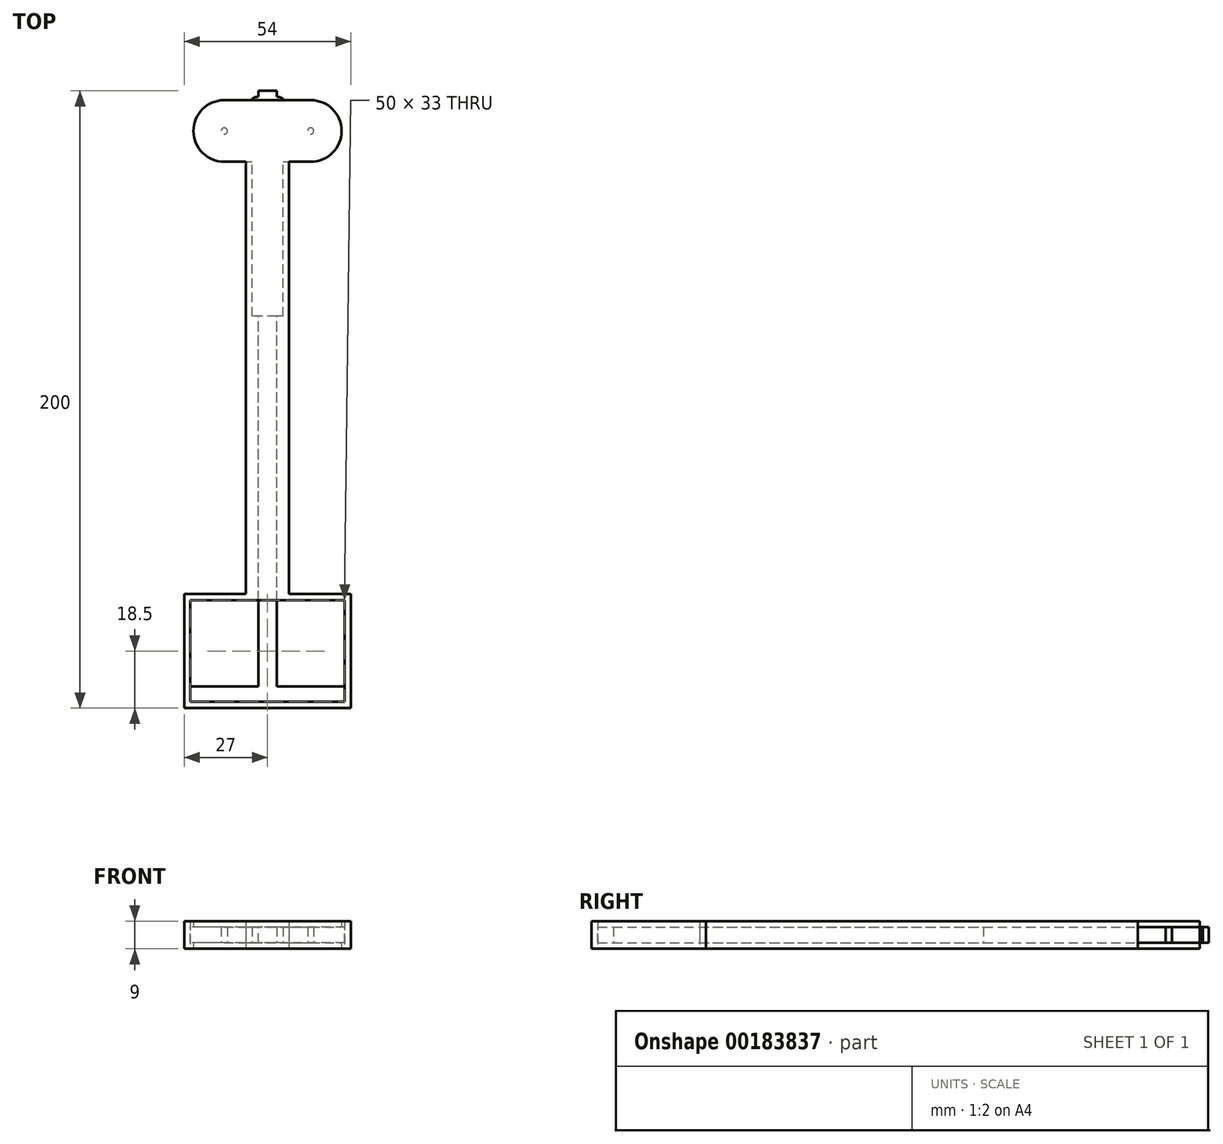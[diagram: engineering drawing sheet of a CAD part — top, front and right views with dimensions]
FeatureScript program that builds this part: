
annotation { "Feature Type Name" : "Feature", "Feature Type Description" : "" }
export const myFeature = defineFeature(function(context is Context, id is Id, definition is map)
    precondition{}
    {
        {
            var Q0;
            Q0=qCreatedBy(makeId("Top.planeOp"),FACE);
            var sketch = newSketch(context, id + "F0", { "sketchPlane" : qUnion([Q0])});
            skLineSegment(sketch, "E0.bottom", {"start": v(0, -180) * mm, "end": v(3, -180) * mm});
            skLineSegment(sketch, "E0.top", {"start": v(0, 13) * mm, "end": v(3, 13) * mm});
            skLineSegment(sketch, "E0.left", {"start": v(0, -180) * mm, "end": v(0, 13) * mm});
            skLineSegment(sketch, "E0.right", {"start": v(3, -180) * mm, "end": v(3, 13) * mm});
            skLineSegment(sketch, "E1", {"start": v(0, 10) * mm, "end": v(3, 10) * mm, "construction": true});
            skArc(sketch, "E2", {"start": v(3, 11.09) * mm, "mid": v(4.04, 10.94) * mm, "end": v(5, 10.5) * mm});
            skLineSegment(sketch, "E3", {"start": v(5, 10.5) * mm, "end": v(5, 10) * mm});
            skArc(sketch, "E4.MirrorCS", {"start": v(3, 8.91) * mm, "mid": v(4.04, 9.06) * mm, "end": v(5, 9.5) * mm});
            skLineSegment(sketch, "E5.MirrorCS", {"start": v(5, 9.5) * mm, "end": v(5, 10) * mm});
            skArc(sketch, "E6.1.0.0", {"start": v(3, 7.89) * mm, "mid": v(4.04, 7.74) * mm, "end": v(5, 7.3) * mm});
            skLineSegment(sketch, "E6.1.0.1", {"start": v(5, 7.3) * mm, "end": v(5, 6.8) * mm});
            skLineSegment(sketch, "E6.1.0.2", {"start": v(5, 6.3) * mm, "end": v(5, 6.8) * mm});
            skArc(sketch, "E6.1.0.3", {"start": v(3, 5.71) * mm, "mid": v(4.04, 5.86) * mm, "end": v(5, 6.3) * mm});
            skArc(sketch, "E6.2.0.0", {"start": v(3, 4.69) * mm, "mid": v(4.04, 4.54) * mm, "end": v(5, 4.1) * mm});
            skLineSegment(sketch, "E6.2.0.1", {"start": v(5, 4.1) * mm, "end": v(5, 3.6) * mm});
            skLineSegment(sketch, "E6.2.0.2", {"start": v(5, 3.1) * mm, "end": v(5, 3.6) * mm});
            skArc(sketch, "E6.2.0.3", {"start": v(3, 2.51) * mm, "mid": v(4.04, 2.66) * mm, "end": v(5, 3.1) * mm});
            skLineSegment(sketch, "E6.direction1", {"start": v(3, 7.39) * mm, "end": v(3, 4.19) * mm, "construction": true});
            skArc(sketch, "E7.0.3.0", {"start": v(3, 1.49) * mm, "mid": v(4.04, 1.34) * mm, "end": v(5, 0.9) * mm});
            skLineSegment(sketch, "E7.4.3.0", {"start": v(5, 0.9) * mm, "end": v(5, 0.4) * mm});
            skLineSegment(sketch, "E7.7.3.0", {"start": v(5, -0.1) * mm, "end": v(5, 0.4) * mm});
            skArc(sketch, "E7.10.3.0", {"start": v(3, -0.69) * mm, "mid": v(4.04, -0.54) * mm, "end": v(5, -0.1) * mm});
            skArc(sketch, "E7.0.4.0", {"start": v(3, -1.71) * mm, "mid": v(4.04, -1.86) * mm, "end": v(5, -2.3) * mm});
            skLineSegment(sketch, "E7.4.4.0", {"start": v(5, -2.3) * mm, "end": v(5, -2.8) * mm});
            skLineSegment(sketch, "E7.7.4.0", {"start": v(5, -3.3) * mm, "end": v(5, -2.8) * mm});
            skArc(sketch, "E7.10.4.0", {"start": v(3, -3.89) * mm, "mid": v(4.04, -3.74) * mm, "end": v(5, -3.3) * mm});
            skArc(sketch, "E7.0.5.0", {"start": v(3, -4.91) * mm, "mid": v(4.04, -5.06) * mm, "end": v(5, -5.5) * mm});
            skLineSegment(sketch, "E7.4.5.0", {"start": v(5, -5.5) * mm, "end": v(5, -6) * mm});
            skLineSegment(sketch, "E7.7.5.0", {"start": v(5, -6.5) * mm, "end": v(5, -6) * mm});
            skArc(sketch, "E7.10.5.0", {"start": v(3, -7.09) * mm, "mid": v(4.04, -6.94) * mm, "end": v(5, -6.5) * mm});
            skArc(sketch, "E7.0.6.0", {"start": v(3, -8.11) * mm, "mid": v(4.04, -8.26) * mm, "end": v(5, -8.7) * mm});
            skLineSegment(sketch, "E7.4.6.0", {"start": v(5, -8.7) * mm, "end": v(5, -9.2) * mm});
            skLineSegment(sketch, "E7.7.6.0", {"start": v(5, -9.7) * mm, "end": v(5, -9.2) * mm});
            skArc(sketch, "E7.10.6.0", {"start": v(3, -10.29) * mm, "mid": v(4.04, -10.14) * mm, "end": v(5, -9.7) * mm});
            skArc(sketch, "E7.0.7.0", {"start": v(3, -11.31) * mm, "mid": v(4.04, -11.46) * mm, "end": v(5, -11.9) * mm});
            skLineSegment(sketch, "E7.4.7.0", {"start": v(5, -11.9) * mm, "end": v(5, -12.4) * mm});
            skLineSegment(sketch, "E7.7.7.0", {"start": v(5, -12.9) * mm, "end": v(5, -12.4) * mm});
            skArc(sketch, "E7.10.7.0", {"start": v(3, -13.49) * mm, "mid": v(4.04, -13.34) * mm, "end": v(5, -12.9) * mm});
            skArc(sketch, "E7.0.8.0", {"start": v(3, -14.51) * mm, "mid": v(4.04, -14.66) * mm, "end": v(5, -15.1) * mm});
            skLineSegment(sketch, "E7.4.8.0", {"start": v(5, -15.1) * mm, "end": v(5, -15.6) * mm});
            skLineSegment(sketch, "E7.7.8.0", {"start": v(5, -16.1) * mm, "end": v(5, -15.6) * mm});
            skArc(sketch, "E7.10.8.0", {"start": v(3, -16.69) * mm, "mid": v(4.04, -16.54) * mm, "end": v(5, -16.1) * mm});
            skArc(sketch, "E7.0.9.0", {"start": v(3, -17.71) * mm, "mid": v(4.04, -17.86) * mm, "end": v(5, -18.3) * mm});
            skLineSegment(sketch, "E7.4.9.0", {"start": v(5, -18.3) * mm, "end": v(5, -18.8) * mm});
            skLineSegment(sketch, "E7.7.9.0", {"start": v(5, -19.3) * mm, "end": v(5, -18.8) * mm});
            skArc(sketch, "E7.10.9.0", {"start": v(3, -19.89) * mm, "mid": v(4.04, -19.74) * mm, "end": v(5, -19.3) * mm});
            skArc(sketch, "E7.0.10.0", {"start": v(3, -20.91) * mm, "mid": v(4.04, -21.06) * mm, "end": v(5, -21.5) * mm});
            skLineSegment(sketch, "E7.4.10.0", {"start": v(5, -21.5) * mm, "end": v(5, -22) * mm});
            skLineSegment(sketch, "E7.7.10.0", {"start": v(5, -22.5) * mm, "end": v(5, -22) * mm});
            skArc(sketch, "E7.10.10.0", {"start": v(3, -23.09) * mm, "mid": v(4.04, -22.94) * mm, "end": v(5, -22.5) * mm});
            skArc(sketch, "E7.0.11.0", {"start": v(3, -24.11) * mm, "mid": v(4.04, -24.26) * mm, "end": v(5, -24.7) * mm});
            skLineSegment(sketch, "E7.4.11.0", {"start": v(5, -24.7) * mm, "end": v(5, -25.2) * mm});
            skLineSegment(sketch, "E7.7.11.0", {"start": v(5, -25.7) * mm, "end": v(5, -25.2) * mm});
            skArc(sketch, "E7.10.11.0", {"start": v(3, -26.29) * mm, "mid": v(4.04, -26.14) * mm, "end": v(5, -25.7) * mm});
            skArc(sketch, "E7.0.12.0", {"start": v(3, -27.31) * mm, "mid": v(4.04, -27.46) * mm, "end": v(5, -27.9) * mm});
            skLineSegment(sketch, "E7.4.12.0", {"start": v(5, -27.9) * mm, "end": v(5, -28.4) * mm});
            skLineSegment(sketch, "E7.7.12.0", {"start": v(5, -28.9) * mm, "end": v(5, -28.4) * mm});
            skArc(sketch, "E7.10.12.0", {"start": v(3, -29.49) * mm, "mid": v(4.04, -29.34) * mm, "end": v(5, -28.9) * mm});
            skArc(sketch, "E7.0.13.0", {"start": v(3, -30.51) * mm, "mid": v(4.04, -30.66) * mm, "end": v(5, -31.1) * mm});
            skLineSegment(sketch, "E7.4.13.0", {"start": v(5, -31.1) * mm, "end": v(5, -31.6) * mm});
            skLineSegment(sketch, "E7.7.13.0", {"start": v(5, -32.1) * mm, "end": v(5, -31.6) * mm});
            skArc(sketch, "E7.10.13.0", {"start": v(3, -32.69) * mm, "mid": v(4.04, -32.54) * mm, "end": v(5, -32.1) * mm});
            skArc(sketch, "E7.0.14.0", {"start": v(3, -33.71) * mm, "mid": v(4.04, -33.86) * mm, "end": v(5, -34.3) * mm});
            skLineSegment(sketch, "E7.4.14.0", {"start": v(5, -34.3) * mm, "end": v(5, -34.8) * mm});
            skLineSegment(sketch, "E7.7.14.0", {"start": v(5, -35.3) * mm, "end": v(5, -34.8) * mm});
            skArc(sketch, "E7.10.14.0", {"start": v(3, -35.89) * mm, "mid": v(4.04, -35.74) * mm, "end": v(5, -35.3) * mm});
            skArc(sketch, "E7.0.15.0", {"start": v(3, -36.91) * mm, "mid": v(4.04, -37.06) * mm, "end": v(5, -37.5) * mm});
            skLineSegment(sketch, "E7.4.15.0", {"start": v(5, -37.5) * mm, "end": v(5, -38) * mm});
            skLineSegment(sketch, "E7.7.15.0", {"start": v(5, -38.5) * mm, "end": v(5, -38) * mm});
            skArc(sketch, "E7.10.15.0", {"start": v(3, -39.09) * mm, "mid": v(4.04, -38.94) * mm, "end": v(5, -38.5) * mm});
            skSolve(sketch);
        }
        {
            var Q0;
            Q0 = qSketchRegion(id + "F0", true);
            extrude(context, id + "F1", {"entities" : qUnion([Q0]), "depth" : 5 * mm});
        }
        {
            var Q0;
            Q0=makeQuery(id+"F1.opExtrude","SWEPT_BODY",BODY,{"disambiguationData":[OSD([sQuery(id+"F0.wireOp",EDGE,"E0.bottom"),sQuery(id+"F0.wireOp",EDGE,"E0.top"),sQuery(id+"F0.wireOp",EDGE,"E0.left"),sQuery(id+"F0.wireOp",EDGE,"E0.right"),sQuery(id+"F0.wireOp",EDGE,"E2"),sQuery(id+"F0.wireOp",EDGE,"E3"),sQuery(id+"F0.wireOp",EDGE,"E4.MirrorCS"),sQuery(id+"F0.wireOp",EDGE,"E5.MirrorCS"),sQuery(id+"F0.wireOp",EDGE,"E6.1.0.0"),sQuery(id+"F0.wireOp",EDGE,"E6.1.0.1"),sQuery(id+"F0.wireOp",EDGE,"E6.1.0.2"),sQuery(id+"F0.wireOp",EDGE,"E6.1.0.3"),sQuery(id+"F0.wireOp",EDGE,"E6.2.0.0"),sQuery(id+"F0.wireOp",EDGE,"E6.2.0.1"),sQuery(id+"F0.wireOp",EDGE,"E6.2.0.2"),sQuery(id+"F0.wireOp",EDGE,"E6.2.0.3"),sQuery(id+"F0.wireOp",EDGE,"E7.0.3.0"),sQuery(id+"F0.wireOp",EDGE,"E7.4.3.0"),sQuery(id+"F0.wireOp",EDGE,"E7.7.3.0"),sQuery(id+"F0.wireOp",EDGE,"E7.10.3.0"),sQuery(id+"F0.wireOp",EDGE,"E7.0.4.0"),sQuery(id+"F0.wireOp",EDGE,"E7.4.4.0"),sQuery(id+"F0.wireOp",EDGE,"E7.7.4.0"),sQuery(id+"F0.wireOp",EDGE,"E7.10.4.0"),sQuery(id+"F0.wireOp",EDGE,"E7.0.5.0"),sQuery(id+"F0.wireOp",EDGE,"E7.4.5.0"),sQuery(id+"F0.wireOp",EDGE,"E7.7.5.0"),sQuery(id+"F0.wireOp",EDGE,"E7.10.5.0"),sQuery(id+"F0.wireOp",EDGE,"E7.0.6.0"),sQuery(id+"F0.wireOp",EDGE,"E7.4.6.0"),sQuery(id+"F0.wireOp",EDGE,"E7.7.6.0"),sQuery(id+"F0.wireOp",EDGE,"E7.10.6.0"),sQuery(id+"F0.wireOp",EDGE,"E7.0.7.0"),sQuery(id+"F0.wireOp",EDGE,"E7.4.7.0"),sQuery(id+"F0.wireOp",EDGE,"E7.7.7.0"),sQuery(id+"F0.wireOp",EDGE,"E7.10.7.0"),sQuery(id+"F0.wireOp",EDGE,"E7.0.8.0"),sQuery(id+"F0.wireOp",EDGE,"E7.4.8.0"),sQuery(id+"F0.wireOp",EDGE,"E7.7.8.0"),sQuery(id+"F0.wireOp",EDGE,"E7.10.8.0"),sQuery(id+"F0.wireOp",EDGE,"E7.0.9.0"),sQuery(id+"F0.wireOp",EDGE,"E7.4.9.0"),sQuery(id+"F0.wireOp",EDGE,"E7.7.9.0"),sQuery(id+"F0.wireOp",EDGE,"E7.10.9.0"),sQuery(id+"F0.wireOp",EDGE,"E7.0.10.0"),sQuery(id+"F0.wireOp",EDGE,"E7.4.10.0"),sQuery(id+"F0.wireOp",EDGE,"E7.7.10.0"),sQuery(id+"F0.wireOp",EDGE,"E7.10.10.0"),sQuery(id+"F0.wireOp",EDGE,"E7.0.11.0"),sQuery(id+"F0.wireOp",EDGE,"E7.4.11.0"),sQuery(id+"F0.wireOp",EDGE,"E7.7.11.0"),sQuery(id+"F0.wireOp",EDGE,"E7.10.11.0"),sQuery(id+"F0.wireOp",EDGE,"E7.0.12.0"),sQuery(id+"F0.wireOp",EDGE,"E7.4.12.0"),sQuery(id+"F0.wireOp",EDGE,"E7.7.12.0"),sQuery(id+"F0.wireOp",EDGE,"E7.10.12.0"),sQuery(id+"F0.wireOp",EDGE,"E7.0.13.0"),sQuery(id+"F0.wireOp",EDGE,"E7.4.13.0"),sQuery(id+"F0.wireOp",EDGE,"E7.7.13.0"),sQuery(id+"F0.wireOp",EDGE,"E7.10.13.0"),sQuery(id+"F0.wireOp",EDGE,"E7.0.14.0"),sQuery(id+"F0.wireOp",EDGE,"E7.4.14.0"),sQuery(id+"F0.wireOp",EDGE,"E7.7.14.0"),sQuery(id+"F0.wireOp",EDGE,"E7.10.14.0"),sQuery(id+"F0.wireOp",EDGE,"E7.0.15.0"),sQuery(id+"F0.wireOp",EDGE,"E7.4.15.0"),sQuery(id+"F0.wireOp",EDGE,"E7.7.15.0"),sQuery(id+"F0.wireOp",EDGE,"E7.10.15.0")])]});
            var Q1;
            Q1=makeQuery(id+"F1.opExtrude","SWEPT_FACE",FACE,{"disambiguationData":[OSD([sQuery(id+"F0.wireOp",EDGE,"E0.left")])]});
            mirror(context, id + "F2", {"operationType" : NewBodyOperationType.ADD, "entities" : qUnion([Q0]), "mirrorPlane" : qUnion([Q1])});
        }
        {
            var Q0;
            {var subQ0=makeQuery(id+"F1.opExtrude","SWEPT_FACE",FACE,{"disambiguationData":[OSD([sQuery(id+"F0.wireOp",EDGE,"E0.bottom")])]});Q0=makeQuery(id+"F2.boolean.opBoolean","MERGE",FACE,{"derivedFrom":[subQ0,makeQuery(id+"F2.opPattern","COPY",FACE,{"derivedFrom":subQ0,"instanceName":"1"})]});}
            var sketch = newSketch(context, id + "F3", { "sketchPlane" : qUnion([Q0])});
            skLineSegment(sketch, "E8.bottom", {"start": v(25, 0) * mm, "end": v(-25, 0) * mm});
            skLineSegment(sketch, "E8.top", {"start": v(25, 5) * mm, "end": v(-25, 5) * mm});
            skLineSegment(sketch, "E8.left", {"start": v(25, 0) * mm, "end": v(25, 5) * mm});
            skLineSegment(sketch, "E8.right", {"start": v(-25, 0) * mm, "end": v(-25, 5) * mm});
            skPoint(sketch, "E8.middle", {"position": v(0, 2.5) * mm});
            skPoint(sketch, "E8.middle.positionSnap0", {"position": v(-3, 2.5) * mm});
            skPoint(sketch, "E8.centerSnap0", {"position": v(-3, 2.5) * mm});
            skSolve(sketch);
        }
        {
            var Q0;
            Q0 = qSketchRegion(id + "F3", true);
            extrude(context, id + "F4", {"entities" : qUnion([Q0]), "operationType" : NewBodyOperationType.ADD, "depth" : 5 * mm});
        }
        {
            var Q0;
            Q0=qCreatedBy(makeId("Top.planeOp"),FACE);
            var sketch = newSketch(context, id + "F5", { "sketchPlane" : qUnion([Q0])});
            skCircle(sketch, "E9", {"center": v(14, 0) * mm, "radius": 10 * mm});
            skLineSegment(sketch, "E10", {"start": v(0, 10) * mm, "end": v(14, 10) * mm});
            skLineSegment(sketch, "E11", {"start": v(14, -10) * mm, "end": v(7, -10) * mm});
            skLineSegment(sketch, "E12", {"start": v(7, -10) * mm, "end": v(7, -150) * mm});
            skLineSegment(sketch, "E13", {"start": v(7, -150) * mm, "end": v(27, -150) * mm});
            skLineSegment(sketch, "E14", {"start": v(27, -150) * mm, "end": v(27, -187) * mm});
            skLineSegment(sketch, "E15", {"start": v(27, -187) * mm, "end": v(0, -187) * mm});
            skLineSegment(sketch, "E16.MirrorCS", {"start": v(0, 10) * mm, "end": v(-14, 10) * mm});
            skCircle(sketch, "E17.MirrorC", {"center": v(-14, 0) * mm, "radius": 10 * mm});
            skLineSegment(sketch, "E18.MirrorCS", {"start": v(-14, -10) * mm, "end": v(-7, -10) * mm});
            skLineSegment(sketch, "E19.MirrorCS", {"start": v(-7, -10) * mm, "end": v(-7, -150) * mm});
            skLineSegment(sketch, "E20.MirrorCS", {"start": v(-7, -150) * mm, "end": v(-27, -150) * mm});
            skLineSegment(sketch, "E21.MirrorCS", {"start": v(-27, -150) * mm, "end": v(-27, -187) * mm});
            skLineSegment(sketch, "E22.MirrorCS", {"start": v(-27, -187) * mm, "end": v(0, -187) * mm});
            skLineSegment(sketch, "E23.bottom", {"start": v(25, -185) * mm, "end": v(-25, -185) * mm});
            skLineSegment(sketch, "E23.top", {"start": v(25, -152) * mm, "end": v(-25, -152) * mm});
            skLineSegment(sketch, "E23.left", {"start": v(25, -185) * mm, "end": v(25, -152) * mm});
            skLineSegment(sketch, "E23.right", {"start": v(-25, -185) * mm, "end": v(-25, -152) * mm});
            skPoint(sketch, "E23.middle", {"position": v(0, -168.5) * mm});
            skSolve(sketch);
        }
        {
            var Q0;
            Q0 = qSketchRegion(id + "F5", true);
            extrude(context, id + "F6", {"entities" : qUnion([Q0]), "depth" : 7 * mm, "hasSecondDirection" : true, "secondDirectionOppositeDirection" : true, "secondDirectionDepth" : 2 * mm});
        }
        {
            var Q0;
            Q0=makeQuery(id+"F1.opExtrude","SWEPT_BODY",BODY,{"disambiguationData":[OSD([sQuery(id+"F0.wireOp",EDGE,"E0.bottom"),sQuery(id+"F0.wireOp",EDGE,"E0.top"),sQuery(id+"F0.wireOp",EDGE,"E0.left"),sQuery(id+"F0.wireOp",EDGE,"E0.right"),sQuery(id+"F0.wireOp",EDGE,"E2"),sQuery(id+"F0.wireOp",EDGE,"E3"),sQuery(id+"F0.wireOp",EDGE,"E4.MirrorCS"),sQuery(id+"F0.wireOp",EDGE,"E5.MirrorCS"),sQuery(id+"F0.wireOp",EDGE,"E6.1.0.0"),sQuery(id+"F0.wireOp",EDGE,"E6.1.0.1"),sQuery(id+"F0.wireOp",EDGE,"E6.1.0.2"),sQuery(id+"F0.wireOp",EDGE,"E6.1.0.3"),sQuery(id+"F0.wireOp",EDGE,"E6.2.0.0"),sQuery(id+"F0.wireOp",EDGE,"E6.2.0.1"),sQuery(id+"F0.wireOp",EDGE,"E6.2.0.2"),sQuery(id+"F0.wireOp",EDGE,"E6.2.0.3"),sQuery(id+"F0.wireOp",EDGE,"E7.0.3.0"),sQuery(id+"F0.wireOp",EDGE,"E7.4.3.0"),sQuery(id+"F0.wireOp",EDGE,"E7.7.3.0"),sQuery(id+"F0.wireOp",EDGE,"E7.10.3.0"),sQuery(id+"F0.wireOp",EDGE,"E7.0.4.0"),sQuery(id+"F0.wireOp",EDGE,"E7.4.4.0"),sQuery(id+"F0.wireOp",EDGE,"E7.7.4.0"),sQuery(id+"F0.wireOp",EDGE,"E7.10.4.0"),sQuery(id+"F0.wireOp",EDGE,"E7.0.5.0"),sQuery(id+"F0.wireOp",EDGE,"E7.4.5.0"),sQuery(id+"F0.wireOp",EDGE,"E7.7.5.0"),sQuery(id+"F0.wireOp",EDGE,"E7.10.5.0"),sQuery(id+"F0.wireOp",EDGE,"E7.0.6.0"),sQuery(id+"F0.wireOp",EDGE,"E7.4.6.0"),sQuery(id+"F0.wireOp",EDGE,"E7.7.6.0"),sQuery(id+"F0.wireOp",EDGE,"E7.10.6.0"),sQuery(id+"F0.wireOp",EDGE,"E7.0.7.0"),sQuery(id+"F0.wireOp",EDGE,"E7.4.7.0"),sQuery(id+"F0.wireOp",EDGE,"E7.7.7.0"),sQuery(id+"F0.wireOp",EDGE,"E7.10.7.0"),sQuery(id+"F0.wireOp",EDGE,"E7.0.8.0"),sQuery(id+"F0.wireOp",EDGE,"E7.4.8.0"),sQuery(id+"F0.wireOp",EDGE,"E7.7.8.0"),sQuery(id+"F0.wireOp",EDGE,"E7.10.8.0"),sQuery(id+"F0.wireOp",EDGE,"E7.0.9.0"),sQuery(id+"F0.wireOp",EDGE,"E7.4.9.0"),sQuery(id+"F0.wireOp",EDGE,"E7.7.9.0"),sQuery(id+"F0.wireOp",EDGE,"E7.10.9.0"),sQuery(id+"F0.wireOp",EDGE,"E7.0.10.0"),sQuery(id+"F0.wireOp",EDGE,"E7.4.10.0"),sQuery(id+"F0.wireOp",EDGE,"E7.7.10.0"),sQuery(id+"F0.wireOp",EDGE,"E7.10.10.0"),sQuery(id+"F0.wireOp",EDGE,"E7.0.11.0"),sQuery(id+"F0.wireOp",EDGE,"E7.4.11.0"),sQuery(id+"F0.wireOp",EDGE,"E7.7.11.0"),sQuery(id+"F0.wireOp",EDGE,"E7.10.11.0"),sQuery(id+"F0.wireOp",EDGE,"E7.0.12.0"),sQuery(id+"F0.wireOp",EDGE,"E7.4.12.0"),sQuery(id+"F0.wireOp",EDGE,"E7.7.12.0"),sQuery(id+"F0.wireOp",EDGE,"E7.10.12.0"),sQuery(id+"F0.wireOp",EDGE,"E7.0.13.0"),sQuery(id+"F0.wireOp",EDGE,"E7.4.13.0"),sQuery(id+"F0.wireOp",EDGE,"E7.7.13.0"),sQuery(id+"F0.wireOp",EDGE,"E7.10.13.0"),sQuery(id+"F0.wireOp",EDGE,"E7.0.14.0"),sQuery(id+"F0.wireOp",EDGE,"E7.4.14.0"),sQuery(id+"F0.wireOp",EDGE,"E7.7.14.0"),sQuery(id+"F0.wireOp",EDGE,"E7.10.14.0"),sQuery(id+"F0.wireOp",EDGE,"E7.0.15.0"),sQuery(id+"F0.wireOp",EDGE,"E7.4.15.0"),sQuery(id+"F0.wireOp",EDGE,"E7.7.15.0"),sQuery(id+"F0.wireOp",EDGE,"E7.10.15.0")])]});
            var Q1;
            Q1=makeQuery(id+"F6.opExtrude","SWEPT_BODY",BODY,{"disambiguationData":[OSD([sQuery(id+"F5.wireOp",EDGE,"E9"),sQuery(id+"F5.wireOp",EDGE,"E10"),sQuery(id+"F5.wireOp",EDGE,"E11"),sQuery(id+"F5.wireOp",EDGE,"E12"),sQuery(id+"F5.wireOp",EDGE,"E13"),sQuery(id+"F5.wireOp",EDGE,"E14"),sQuery(id+"F5.wireOp",EDGE,"E15"),sQuery(id+"F5.wireOp",EDGE,"E16.MirrorCS"),sQuery(id+"F5.wireOp",EDGE,"E17.MirrorC"),sQuery(id+"F5.wireOp",EDGE,"E18.MirrorCS"),sQuery(id+"F5.wireOp",EDGE,"E19.MirrorCS"),sQuery(id+"F5.wireOp",EDGE,"E20.MirrorCS"),sQuery(id+"F5.wireOp",EDGE,"E21.MirrorCS"),sQuery(id+"F5.wireOp",EDGE,"E22.MirrorCS"),sQuery(id+"F5.wireOp",EDGE,"E23.bottom"),sQuery(id+"F5.wireOp",EDGE,"E23.top"),sQuery(id+"F5.wireOp",EDGE,"E23.left"),sQuery(id+"F5.wireOp",EDGE,"E23.right")])]});
            booleanBodies(context, id + "F7", {"operationType" : BooleanOperationType.SUBTRACTION, "tools" : qUnion([Q0]), "targets" : qUnion([Q1]), "keepTools" : true});
        }
        {
            var Q0;
            Q0=qCreatedBy(makeId("Top.planeOp"),FACE);
            var sketch = newSketch(context, id + "F8", { "sketchPlane" : qUnion([Q0])});
            skArc(sketch, "E24.0", {"start": v(-14, -10) * mm, "mid": v(-24, 0) * mm, "end": v(-14, 10) * mm});
            skLineSegment(sketch, "E25.0", {"start": v(-14, 10) * mm, "end": v(14, 10) * mm});
            skArc(sketch, "E26.0", {"start": v(14, -10) * mm, "mid": v(24, 0) * mm, "end": v(14, 10) * mm});
            skLineSegment(sketch, "E27", {"start": v(-14, -10) * mm, "end": v(14, -10) * mm});
            skSolve(sketch);
        }
        {
            var Q0;
            Q0 = qSketchRegion(id + "F8", true);
            extrude(context, id + "F9", {"entities" : qUnion([Q0]), "operationType" : NewBodyOperationType.REMOVE, "depth" : 5 * mm});
        }
        {
            var Q0;
            {var subQ70=sQuery(id+"F8.wireOp",EDGE,"E27");Q0=makeQuery(id+"F9.boolean.opBoolean","COPY",FACE,{"disambiguationData":[TD([makeQuery(id+"F6.opExtrude","SWEPT_FACE",FACE,{"disambiguationData":[OSD([sQuery(id+"F5.wireOp",EDGE,"E18.MirrorCS")])]})])],"derivedFrom":makeQuery(id+"F9.opExtrude","SWEPT_FACE",FACE,{"disambiguationData":[OSD([subQ70])]})});}
            var sketch = newSketch(context, id + "F10", { "sketchPlane" : qUnion([Q0])});
            skLineSegment(sketch, "E28.bottom", {"start": v(-5, 5) * mm, "end": v(5, 5) * mm});
            skLineSegment(sketch, "E28.top", {"start": v(-5, 0) * mm, "end": v(5, 0) * mm});
            skLineSegment(sketch, "E28.left", {"start": v(-5, 5) * mm, "end": v(-5, 0) * mm});
            skLineSegment(sketch, "E28.right", {"start": v(5, 5) * mm, "end": v(5, 0) * mm});
            skSolve(sketch);
        }
        {
            var Q0;
            Q0 = qSketchRegion(id + "F10", true);
            extrude(context, id + "F11", {"entities" : qUnion([Q0]), "operationType" : NewBodyOperationType.REMOVE, "oppositeDirection" : true, "depth" : 50 * mm});
        }
        {
            var Q0;
            {var subQ0=makeQuery(id+"F1.opExtrude","CAP_FACE",FACE,{"disambiguationData":[OSD([sQuery(id+"F0.wireOp",EDGE,"E0.bottom"),sQuery(id+"F0.wireOp",EDGE,"E0.top"),sQuery(id+"F0.wireOp",EDGE,"E0.left"),sQuery(id+"F0.wireOp",EDGE,"E0.right"),sQuery(id+"F0.wireOp",EDGE,"E2"),sQuery(id+"F0.wireOp",EDGE,"E3"),sQuery(id+"F0.wireOp",EDGE,"E4.MirrorCS"),sQuery(id+"F0.wireOp",EDGE,"E5.MirrorCS"),sQuery(id+"F0.wireOp",EDGE,"E6.1.0.0"),sQuery(id+"F0.wireOp",EDGE,"E6.1.0.1"),sQuery(id+"F0.wireOp",EDGE,"E6.1.0.2"),sQuery(id+"F0.wireOp",EDGE,"E6.1.0.3"),sQuery(id+"F0.wireOp",EDGE,"E6.2.0.0"),sQuery(id+"F0.wireOp",EDGE,"E6.2.0.1"),sQuery(id+"F0.wireOp",EDGE,"E6.2.0.2"),sQuery(id+"F0.wireOp",EDGE,"E6.2.0.3"),sQuery(id+"F0.wireOp",EDGE,"E7.0.3.0"),sQuery(id+"F0.wireOp",EDGE,"E7.4.3.0"),sQuery(id+"F0.wireOp",EDGE,"E7.7.3.0"),sQuery(id+"F0.wireOp",EDGE,"E7.10.3.0"),sQuery(id+"F0.wireOp",EDGE,"E7.0.4.0"),sQuery(id+"F0.wireOp",EDGE,"E7.4.4.0"),sQuery(id+"F0.wireOp",EDGE,"E7.7.4.0"),sQuery(id+"F0.wireOp",EDGE,"E7.10.4.0"),sQuery(id+"F0.wireOp",EDGE,"E7.0.5.0"),sQuery(id+"F0.wireOp",EDGE,"E7.4.5.0"),sQuery(id+"F0.wireOp",EDGE,"E7.7.5.0"),sQuery(id+"F0.wireOp",EDGE,"E7.10.5.0"),sQuery(id+"F0.wireOp",EDGE,"E7.0.6.0"),sQuery(id+"F0.wireOp",EDGE,"E7.4.6.0"),sQuery(id+"F0.wireOp",EDGE,"E7.7.6.0"),sQuery(id+"F0.wireOp",EDGE,"E7.10.6.0"),sQuery(id+"F0.wireOp",EDGE,"E7.0.7.0"),sQuery(id+"F0.wireOp",EDGE,"E7.4.7.0"),sQuery(id+"F0.wireOp",EDGE,"E7.7.7.0"),sQuery(id+"F0.wireOp",EDGE,"E7.10.7.0"),sQuery(id+"F0.wireOp",EDGE,"E7.0.8.0"),sQuery(id+"F0.wireOp",EDGE,"E7.4.8.0"),sQuery(id+"F0.wireOp",EDGE,"E7.7.8.0"),sQuery(id+"F0.wireOp",EDGE,"E7.10.8.0"),sQuery(id+"F0.wireOp",EDGE,"E7.0.9.0"),sQuery(id+"F0.wireOp",EDGE,"E7.4.9.0"),sQuery(id+"F0.wireOp",EDGE,"E7.7.9.0"),sQuery(id+"F0.wireOp",EDGE,"E7.10.9.0"),sQuery(id+"F0.wireOp",EDGE,"E7.0.10.0"),sQuery(id+"F0.wireOp",EDGE,"E7.4.10.0"),sQuery(id+"F0.wireOp",EDGE,"E7.7.10.0"),sQuery(id+"F0.wireOp",EDGE,"E7.10.10.0"),sQuery(id+"F0.wireOp",EDGE,"E7.0.11.0"),sQuery(id+"F0.wireOp",EDGE,"E7.4.11.0"),sQuery(id+"F0.wireOp",EDGE,"E7.7.11.0"),sQuery(id+"F0.wireOp",EDGE,"E7.10.11.0"),sQuery(id+"F0.wireOp",EDGE,"E7.0.12.0"),sQuery(id+"F0.wireOp",EDGE,"E7.4.12.0"),sQuery(id+"F0.wireOp",EDGE,"E7.7.12.0"),sQuery(id+"F0.wireOp",EDGE,"E7.10.12.0"),sQuery(id+"F0.wireOp",EDGE,"E7.0.13.0"),sQuery(id+"F0.wireOp",EDGE,"E7.4.13.0"),sQuery(id+"F0.wireOp",EDGE,"E7.7.13.0"),sQuery(id+"F0.wireOp",EDGE,"E7.10.13.0"),sQuery(id+"F0.wireOp",EDGE,"E7.0.14.0"),sQuery(id+"F0.wireOp",EDGE,"E7.4.14.0"),sQuery(id+"F0.wireOp",EDGE,"E7.7.14.0"),sQuery(id+"F0.wireOp",EDGE,"E7.10.14.0"),sQuery(id+"F0.wireOp",EDGE,"E7.0.15.0"),sQuery(id+"F0.wireOp",EDGE,"E7.4.15.0"),sQuery(id+"F0.wireOp",EDGE,"E7.7.15.0"),sQuery(id+"F0.wireOp",EDGE,"E7.10.15.0")])],"isStart":true});Q0=makeQuery(id+"F11.boolean.opBoolean","MERGE",FACE,{"derivedFrom":[makeQuery(id+"F9.boolean.opBoolean","MERGE",FACE,{"derivedFrom":[makeQuery(id+"F7.opBoolean","COPY",FACE,{"derivedFrom":makeQuery(id+"F4.boolean.opBoolean","MERGE",FACE,{"derivedFrom":[makeQuery(id+"F2.boolean.opBoolean","MERGE",FACE,{"derivedFrom":[subQ0,makeQuery(id+"F2.opPattern","COPY",FACE,{"derivedFrom":subQ0,"instanceName":"1"})]}),makeQuery(id+"F4.opExtrude","SWEPT_FACE",FACE,{"disambiguationData":[OSD([sQuery(id+"F3.wireOp",EDGE,"E8.bottom")])]})]})}),makeQuery(id+"F9.opExtrude","CAP_FACE",FACE,{"disambiguationData":[OSD([sQuery(id+"F8.wireOp",EDGE,"E24.0"),sQuery(id+"F8.wireOp",EDGE,"E25.0"),sQuery(id+"F8.wireOp",EDGE,"E26.0"),sQuery(id+"F8.wireOp",EDGE,"E27")])],"isStart":true})]}),makeQuery(id+"F11.opExtrude","SWEPT_FACE",FACE,{"disambiguationData":[OSD([sQuery(id+"F10.wireOp",EDGE,"E28.top")])]})]});}
            var sketch = newSketch(context, id + "F12", { "sketchPlane" : qUnion([Q0])});
            skCircle(sketch, "E29", {"center": v(-14, 0) * mm, "radius": 1 * mm});
            skCircle(sketch, "E30", {"center": v(14, 0) * mm, "radius": 1 * mm});
            skSolve(sketch);
        }
        {
            var Q0;
            Q0 = qSketchRegion(id + "F12", true);
            extrude(context, id + "F13", {"entities" : qUnion([Q0]), "operationType" : NewBodyOperationType.ADD, "endBound" : BoundingType.UP_TO_NEXT, "depth" : 25 * mm});
        }
    });
